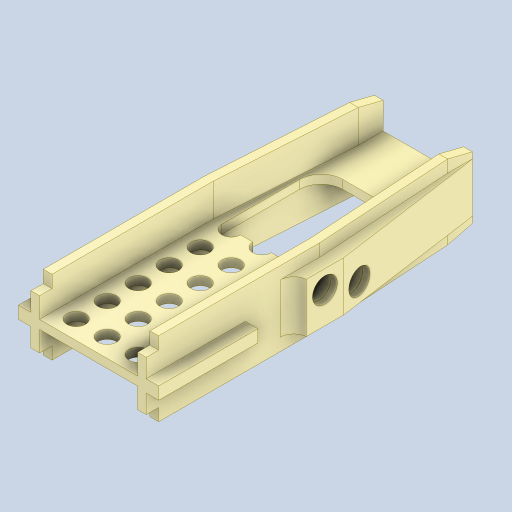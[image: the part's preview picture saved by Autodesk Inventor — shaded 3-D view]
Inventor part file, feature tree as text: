
AUTODESK INVENTOR PART (.ipt)
format: ipt  version: 2023.5 (Build 275446000, 446)  size: 471,040 bytes
history: native  units: mm
features: extrude x12, other x4, fillet x2, mirror x2, pattern_linear x1, pattern_circular x1
ambient origin geometry x8: Origin, YZ Plane, XZ Plane, XY Plane, X Axis, Y Axis, Z Axis, Center Point
bodies: Solid1 (feature_tree)
feature tree (22):
  other  "Sk:Base"
  extrude  "Ex:Midline"  Depth=3.95mm
  extrude  "Ex:FrontSupport"  Depth=14.0mm
  extrude  "Ex:SideRidge"  TaperAngle=0.0deg  [1 undecoded]
  extrude  "Ex:SideWall"  Depth=3.25mm
  extrude  "Ex:BaseHole"  TaperAngle=0.0deg  [1 undecoded]
  pattern_linear  "Pat:BaseHoles"  Spacing1=0.0mm  [1 undecoded]
  fillet  "Fillet:Support"  Radius=3.0mm
  extrude  "Ex:Widening"  Depth=0.7mm
  fillet  "Fillet:Side"  Radius=7.0mm
  extrude  "Ex:FrontTaper"  Depth=11.0mm
  extrude  "Ex:LidNotch"  Depth=1.5mm
  mirror  "Mirror1"
  mirror  "Mirror2"
  other  "Sk:ThreadHole1"
  other  "Sk:ThreadHole2"
  extrude  "Ex:ThreadHole1"  Depth=1.5mm
  extrude  "Ex:ThreadEntry1"  Depth=5.3mm TaperAngle=0.0deg
  extrude  "Ex:ThreadHole2"  Depth=2.5mm
  extrude  "Ex:ThreadEntry2"  Depth=2.5mm
  pattern_circular  "Pat:Threads"  [2 undecoded]
  other  "Sk:LidNotch"
note: 5 required parameter values undecoded (feature->parameter linkage not recoverable at this tier; creation-order binding heuristic only, values carry confidence <= 0.55)
